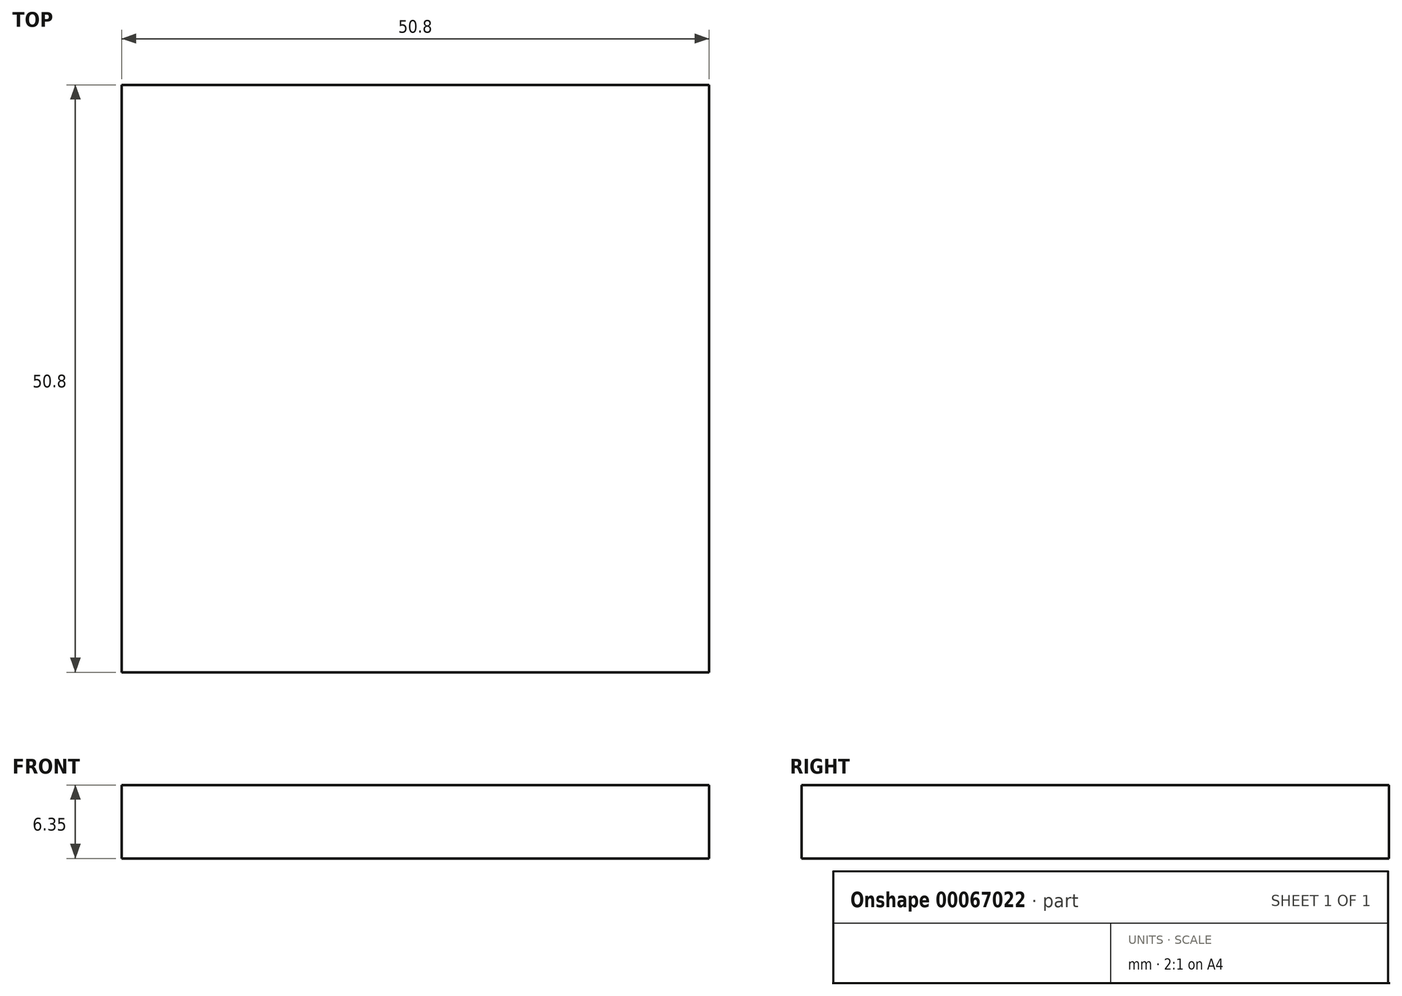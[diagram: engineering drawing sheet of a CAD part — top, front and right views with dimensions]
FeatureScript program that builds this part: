
annotation { "Feature Type Name" : "Feature", "Feature Type Description" : "" }
export const myFeature = defineFeature(function(context is Context, id is Id, definition is map)
    precondition{}
    {
        {
            var Q0;
            Q0=qCreatedBy(makeId("Top.planeOp"),FACE);
            var sketch = newSketch(context, id + "F0", { "sketchPlane" : qUnion([Q0])});
            skLineSegment(sketch, "E0.rect.bottom", {"start": v(-25.4, -25.4) * mm, "end": v(25.4, -25.4) * mm});
            skLineSegment(sketch, "E0.rect.top", {"start": v(-25.4, 25.4) * mm, "end": v(25.4, 25.4) * mm});
            skLineSegment(sketch, "E0.rect.left", {"start": v(-25.4, -25.4) * mm, "end": v(-25.4, 25.4) * mm});
            skLineSegment(sketch, "E0.rect.right", {"start": v(25.4, -25.4) * mm, "end": v(25.4, 25.4) * mm});
            skPoint(sketch, "E0.rect.middle", {"position": v(0, 0) * mm});
            skSolve(sketch);
        }
        {
            var Q0;
            Q0=makeQuery(id+"F0.imprint","IMPRINT",FACE,{"disambiguationData":[TD([[makeQuery(id+"F0.imprint","IMPRINT",EDGE,{"derivedFrom":sQuery(id+"F0.wireOp",EDGE,"E0.rect.bottom")}),1.0]])]});
            extrude(context, id + "F2", {"entities" : qUnion([Q0]), "depth" : 6.35 * mm});
        }
    });
